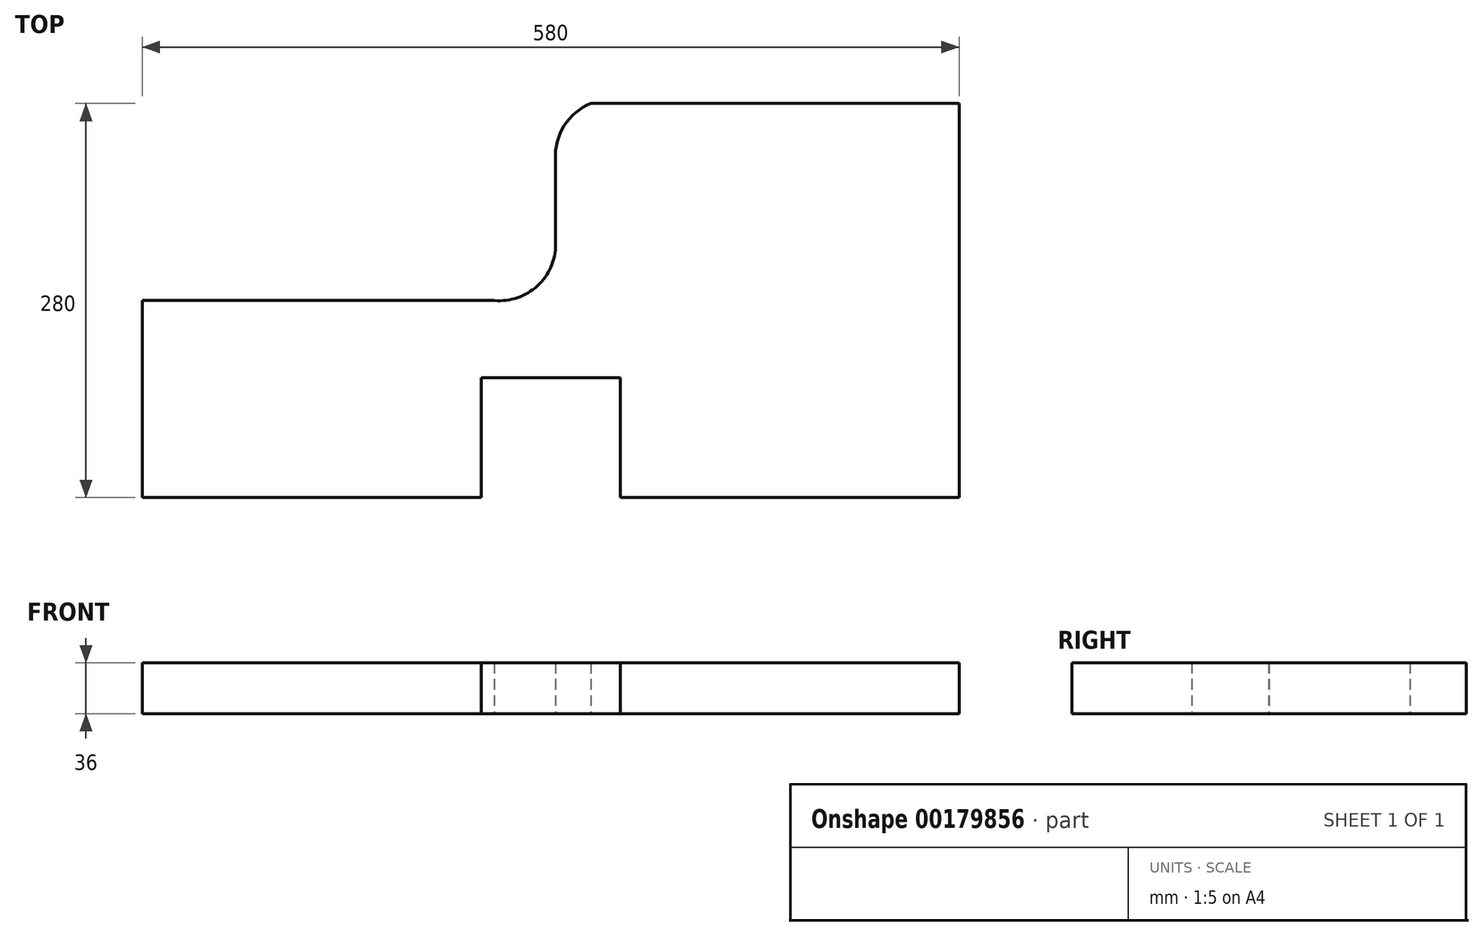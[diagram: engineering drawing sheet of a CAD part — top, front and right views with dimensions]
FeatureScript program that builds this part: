
annotation { "Feature Type Name" : "Feature", "Feature Type Description" : "" }
export const myFeature = defineFeature(function(context is Context, id is Id, definition is map)
    precondition{}
    {
        {
            var Q0;
            Q0=qCreatedBy(makeId("Top.planeOp"),FACE);
            var sketch = newSketch(context, id + "F0", { "sketchPlane" : qUnion([Q0])});
            skLineSegment(sketch, "E0", {"start": v(-296.64, -162.46) * mm, "end": v(-296.64, -22.46) * mm});
            skLineSegment(sketch, "E1", {"start": v(283.36, 117.54) * mm, "end": v(283.36, -162.46) * mm});
            skLineSegment(sketch, "E2", {"start": v(283.36, -162.46) * mm, "end": v(-296.64, -162.46) * mm});
            skLineSegment(sketch, "E3", {"start": v(-46.64, -47.62) * mm, "end": v(-46.64, 142.6) * mm, "construction": true});
            skLineSegment(sketch, "E4", {"start": v(-46.64, 17.54) * mm, "end": v(18.48, 17.54) * mm, "construction": true});
            skArc(sketch, "E5", {"start": v(-46.64, -22.46) * mm, "mid": v(-16.11, -12.03) * mm, "end": v(-3.22, 17.54) * mm});
            skLineSegment(sketch, "E6", {"start": v(-3.22, 77.54) * mm, "end": v(21.95, 77.54) * mm, "construction": true});
            skLineSegment(sketch, "E7", {"start": v(21.95, 77.54) * mm, "end": v(21.95, 117.54) * mm, "construction": true});
            skArc(sketch, "E8", {"start": v(21.95, 117.54) * mm, "mid": v(2.83, 101.65) * mm, "end": v(-3.22, 77.54) * mm});
            skLineSegment(sketch, "E9", {"start": v(-296.64, -22.46) * mm, "end": v(-46.64, -22.46) * mm});
            skLineSegment(sketch, "E10", {"start": v(-3.22, 17.54) * mm, "end": v(-3.22, 77.54) * mm});
            skLineSegment(sketch, "E11", {"start": v(21.95, 117.54) * mm, "end": v(283.36, 117.54) * mm});
            skLineSegment(sketch, "E12", {"start": v(-55.89, -162.46) * mm, "end": v(-55.89, -77.46) * mm});
            skLineSegment(sketch, "E13", {"start": v(-55.89, -77.46) * mm, "end": v(42.61, -77.46) * mm});
            skLineSegment(sketch, "E14", {"start": v(42.61, -77.46) * mm, "end": v(42.61, -162.46) * mm});
            skLineSegment(sketch, "E15", {"start": v(42.61, -162.46) * mm, "end": v(-55.89, -162.46) * mm});
            skLineSegment(sketch, "E16", {"start": v(-6.64, -77.46) * mm, "end": v(-6.64, -162.46) * mm, "construction": true});
            skSolve(sketch);
        }
        {
            var Q0;
            Q0=makeQuery(id+"F0.imprint","IMPRINT",FACE,{"disambiguationData":[TD([[makeQuery(id+"F0.imprint","IMPRINT",EDGE,{"derivedFrom":sQuery(id+"F0.wireOp",EDGE,"E0")}),-1.0]])]});
            extrude(context, id + "F1", {"entities" : qUnion([Q0]), "depth" : 36 * mm});
        }
    });
